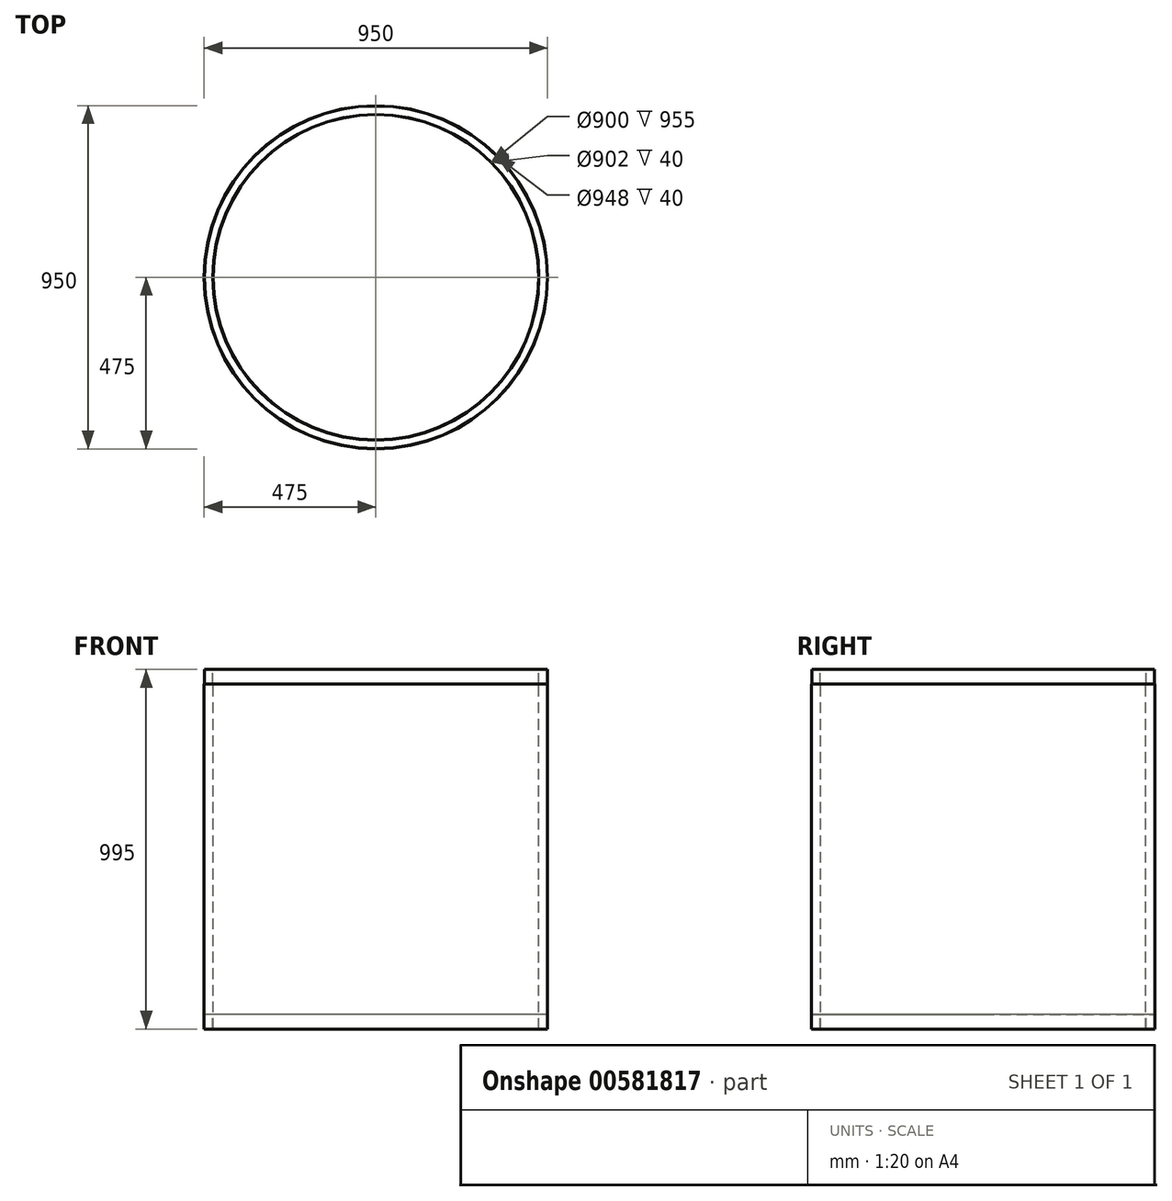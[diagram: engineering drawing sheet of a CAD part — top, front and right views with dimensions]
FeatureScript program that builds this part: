
annotation { "Feature Type Name" : "Feature", "Feature Type Description" : "" }
export const myFeature = defineFeature(function(context is Context, id is Id, definition is map)
    precondition{}
    {
        {
            var Q0;
            Q0=qCreatedBy(makeId("Front.planeOp"),FACE);
            var sketch = newSketch(context, id + "F0", { "sketchPlane" : qUnion([Q0])});
            skLineSegment(sketch, "E0", {"start": v(0, 345.75) * mm, "end": v(0, -558.03) * mm, "construction": true});
            skLineSegment(sketch, "E1", {"start": v(-450, -518.84) * mm, "end": v(-450, 436.16) * mm});
            skLineSegment(sketch, "E2", {"start": v(-450, 436.16) * mm, "end": v(-451, 436.16) * mm});
            skLineSegment(sketch, "E3", {"start": v(-451, 436.16) * mm, "end": v(-451, 476.16) * mm});
            skLineSegment(sketch, "E4", {"start": v(-451, 476.16) * mm, "end": v(-474, 476.16) * mm});
            skLineSegment(sketch, "E5", {"start": v(-474, 476.16) * mm, "end": v(-474, 436.16) * mm});
            skLineSegment(sketch, "E6", {"start": v(-474, 436.16) * mm, "end": v(-475, 436.16) * mm});
            skLineSegment(sketch, "E7", {"start": v(-475, 436.16) * mm, "end": v(-475, -518.84) * mm});
            skLineSegment(sketch, "E8", {"start": v(-475, -518.84) * mm, "end": v(-474, -518.84) * mm});
            skLineSegment(sketch, "E9", {"start": v(-474, -518.84) * mm, "end": v(-474, -478.84) * mm});
            skLineSegment(sketch, "E10", {"start": v(-474, -478.84) * mm, "end": v(-451, -478.84) * mm});
            skLineSegment(sketch, "E11", {"start": v(-451, -478.84) * mm, "end": v(-451, -518.84) * mm});
            skLineSegment(sketch, "E12", {"start": v(-451, -518.84) * mm, "end": v(-450, -518.84) * mm});
            skSolve(sketch);
        }
        {
            var Q0;
            Q0 = qSketchRegion(id + "F0", true);
            var Q1;
            Q1=sQuery(id+"F0.wireOp",EDGE,"E0");
            revolve(context, id + "F1", {"entities" : qUnion([Q0]), "axis" : qUnion([Q1]), "revolveType" : RevolveType.FULL});
        }
    });
